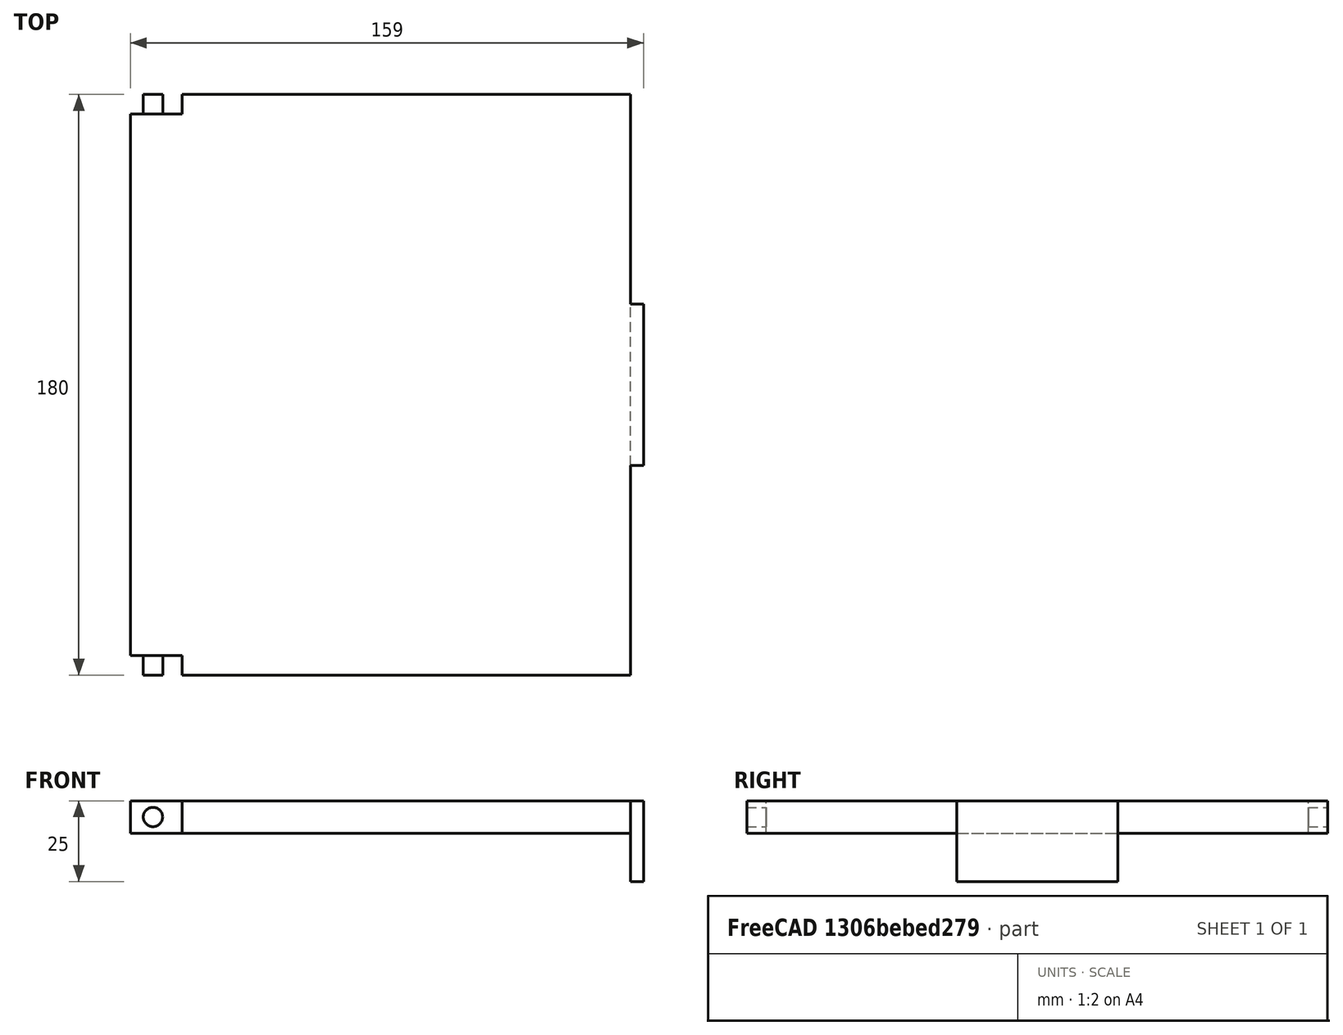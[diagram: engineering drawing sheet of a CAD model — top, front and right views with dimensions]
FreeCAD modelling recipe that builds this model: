
FCSTD DOCUMENT  (FreeCAD 1.0R38806 (Git))
Label: Tapa_sola
License: All rights reserved
LicenseURL: https://en.wikipedia.org/wiki/All_rights_reserved
objects: Part::Box×8, Part::Cut×6, Part::Fuse×3, Part::Cylinder×2
note: 19 computed .brp shape members not serialized (recipe doc carries the construction recipe); baked Part::Feature solids carry a one-line shape summary decoded from their .brp

FEATURE [Part::Box] Box  label="Cube"
  AttacherType = Attacher::AttachEngine3D
  Height = 170
  Length = 155
  Width = 180
FEATURE [Part::Box] Box001  label="Cube001"
  AttacherType = Attacher::AttachEngine3D
  Height = 200
  Length = 145
  Placement = pos=(5,5,5) rot=(0,0,1;0rad)
  Width = 170
FEATURE [Part::Box] Box002  label="tapa"
  AttacherType = Attacher::AttachEngine3D
  Height = 10
  Length = 155
  Placement = pos=(0,0,170) rot=(0,0,1;0rad)
  Width = 180
FEATURE [Part::Box] Box003  label="Agujero"
  AttacherType = Attacher::AttachEngine3D
  Height = 15
  Length = 25
  Placement = pos=(10,-7,5) rot=(0,0,1;0rad)
  Width = 25
FEATURE [Part::Box] Box004  label="Cube002"
  AttacherType = Attacher::AttachEngine3D
  Height = 25
  Length = 4
  Placement = pos=(155,65,155) rot=(0,0,1;0rad)
  Width = 50
FEATURE [Part::Box] Box005  label="Cube003"
  AttacherType = Attacher::AttachEngine3D
  Height = 20
  Length = 12
  Placement = pos=(146,85,130) rot=(0,0,1;0rad)
  Width = 10
FEATURE [Part::Box] Box006  label="visagra_1_1"
  AttacherType = Attacher::AttachEngine3D
  Height = 10
  Length = 16
  Placement = pos=(0,174,170) rot=(0,0,1;0rad)
  Width = 6
FEATURE [Part::Box] Box007  label="visagra2_1"
  AttacherType = Attacher::AttachEngine3D
  Height = 10
  Length = 16
  Placement = pos=(0,0,170) rot=(0,0,1;0rad)
  Width = 6
FEATURE [Part::Cut] Cut  label="EStructura"
  Base = -> Box
  Refine = true
  Tool = -> Box001
FEATURE [Part::Cut] Cut001  label="Caja_p1"
  Base = -> Cut
  Refine = true
  Tool = -> Box003
FEATURE [Part::Cut] Cut002  label="Caja"
  Base = -> Cut001
  Refine = true
  Tool = -> Box005
FEATURE [Part::Cylinder] Cylinder
  Angle = 360
  AttacherType = Attacher::AttachEngine3D
  FirstAngle = 0
  Height = 148
  Placement = pos=(7,192,175) rot=(1,0,0;1.5708rad)
  Radius = 3
  SecondAngle = 0
FEATURE [Part::Cut] Cut003  label="visagra1"
  Base = -> Box006
  Refine = true
  Tool = -> Cylinder
FEATURE [Part::Cylinder] Cylinder001
  Angle = 360
  AttacherType = Attacher::AttachEngine3D
  FirstAngle = 0
  Height = 148
  Placement = pos=(7,139,175) rot=(1,0,0;1.5708rad)
  Radius = 3
  SecondAngle = 0
FEATURE [Part::Cut] Cut004  label="visagra2"
  Base = -> Box007
  Refine = true
  Tool = -> Cylinder001
FEATURE [Part::Fuse] Fusion  label="Tapa_1"
  Base = -> Box002
  Refine = true
  Tool = -> Box004
FEATURE [Part::Fuse] Fusion001
  Base = -> Cut002
  Refine = true
  Tool = -> Cut003
FEATURE [Part::Fuse] Fusion002
  Base = -> Fusion001
  Refine = true
  Tool = -> Cut004
FEATURE [Part::Cut] Cut005  label="Tapa"
  Base = -> Fusion
  Refine = true
  Tool = -> Fusion002
